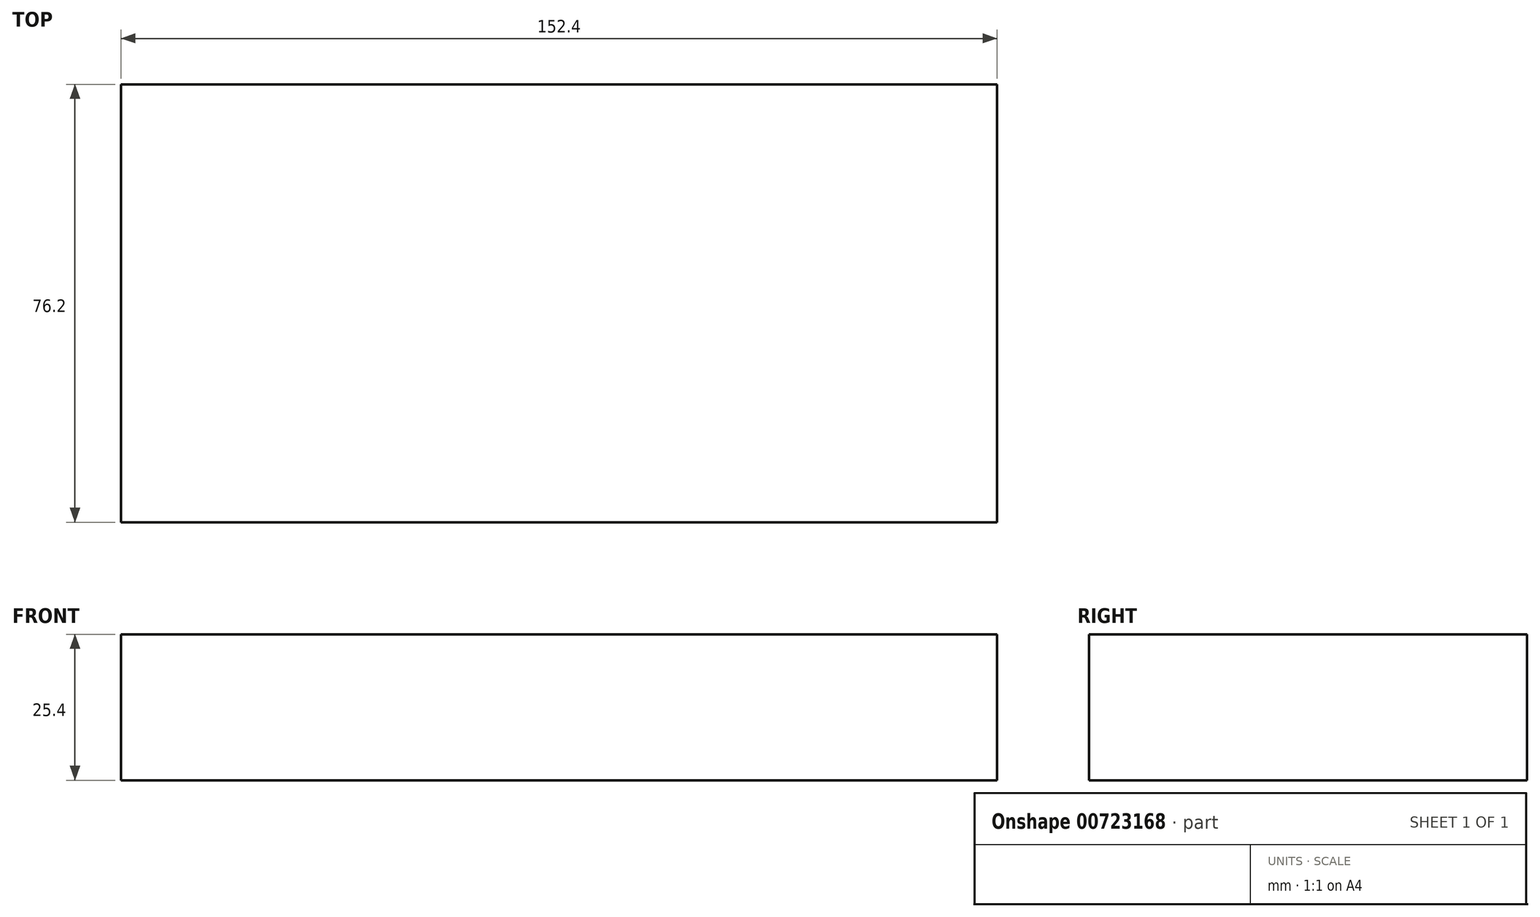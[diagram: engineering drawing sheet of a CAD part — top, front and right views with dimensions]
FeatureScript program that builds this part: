
annotation { "Feature Type Name" : "Feature", "Feature Type Description" : "" }
export const myFeature = defineFeature(function(context is Context, id is Id, definition is map)
    precondition{}
    {
        {
            var Q0;
            Q0=qCreatedBy(makeId("Top.planeOp"),FACE);
            var sketch = newSketch(context, id + "F0", { "sketchPlane" : qUnion([Q0])});
            skLineSegment(sketch, "E0.bottom", {"start": v(76.2, -38.1) * mm, "end": v(-76.2, -38.1) * mm});
            skLineSegment(sketch, "E0.top", {"start": v(76.2, 38.1) * mm, "end": v(-76.2, 38.1) * mm});
            skLineSegment(sketch, "E0.left", {"start": v(76.2, -38.1) * mm, "end": v(76.2, 38.1) * mm});
            skLineSegment(sketch, "E0.right", {"start": v(-76.2, -38.1) * mm, "end": v(-76.2, 38.1) * mm});
            skPoint(sketch, "E0.middle", {"position": v(0, 0) * mm});
            skSolve(sketch);
        }
        {
            var Q0;
            Q0 = qSketchRegion(id + "F0", true);
            extrude(context, id + "F1", {"entities" : qUnion([Q0]), "depth" : 25.4 * mm, "offsetDistance" : 25.4 * mm});
        }
    });
